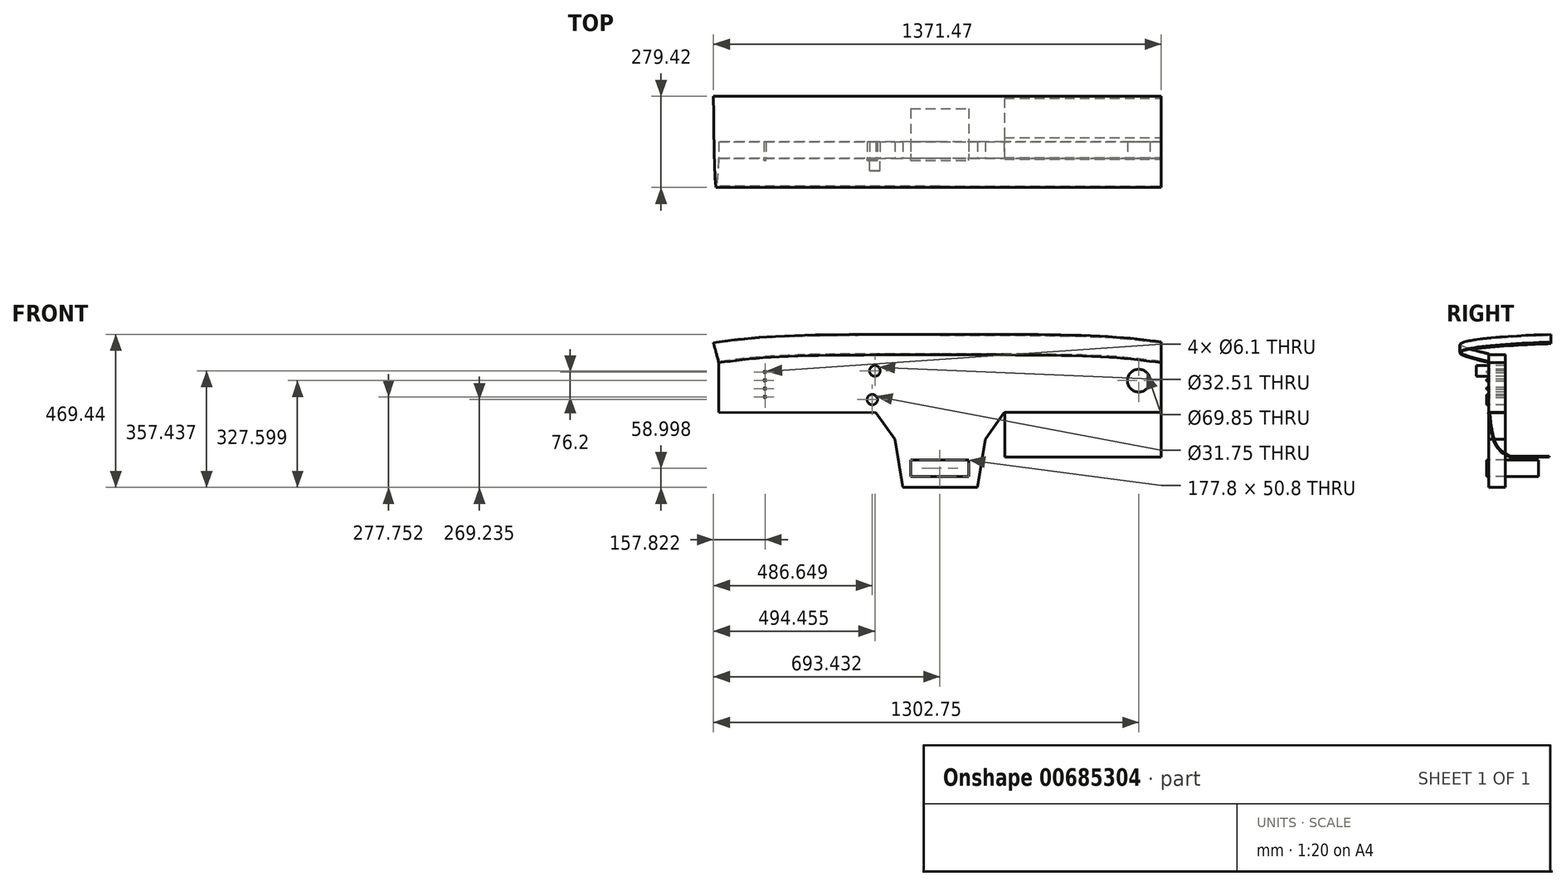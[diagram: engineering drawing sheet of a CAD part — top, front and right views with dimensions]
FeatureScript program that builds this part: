
annotation { "Feature Type Name" : "Feature", "Feature Type Description" : "" }
export const myFeature = defineFeature(function(context is Context, id is Id, definition is map)
    precondition{}
    {
        {
            var Q0;
            Q0=qCreatedBy(makeId("Front.planeOp"),FACE);
            var sketch = newSketch(context, id + "F0", { "sketchPlane" : qUnion([Q0])});
            skLineSegment(sketch, "E0.bottom", {"start": v(-257.56, -56.13) * mm, "end": v(28.19, -56.13) * mm});
            skLineSegment(sketch, "E0.top", {"start": v(-257.56, -106.93) * mm, "end": v(28.19, -106.93) * mm});
            skLineSegment(sketch, "E0.left", {"start": v(-257.56, -56.13) * mm, "end": v(-257.56, -106.93) * mm});
            skLineSegment(sketch, "E0.right", {"start": v(28.19, -56.13) * mm, "end": v(28.19, -106.93) * mm});
            skCircle(sketch, "E1", {"center": v(-226.15, -8.02) * mm, "radius": 26.2 * mm});
            skCircle(sketch, "E2", {"center": v(-154.96, -8.02) * mm, "radius": 26.2 * mm});
            skCircle(sketch, "E3", {"center": v(-83.6, -8.02) * mm, "radius": 26.2 * mm});
            skCircle(sketch, "E4", {"center": v(-11.74, -8.01) * mm, "radius": 26.2 * mm});
            skPoint(sketch, "E5.startSnap0", {"position": v(-118.95, 106.5) * mm});
            skCircle(sketch, "E6", {"center": v(-727.7, 27.7) * mm, "radius": 34.93 * mm});
            skCircle(sketch, "E7", {"center": v(-567.92, 12.4) * mm, "radius": 50.8 * mm});
            skCircle(sketch, "E8", {"center": v(-423.48, 13.97) * mm, "radius": 50.8 * mm});
            skPoint(sketch, "E9.visualSharp", {"position": v(-299.01, -120.46) * mm});
            skPoint(sketch, "E10.visualSharp", {"position": v(72.46, -120.46) * mm});
            skLineSegment(sketch, "E11.bottom", {"start": v(-271.26, 87.77) * mm, "end": v(33.54, 87.77) * mm});
            skLineSegment(sketch, "E11.top", {"start": v(-271.26, 27.37) * mm, "end": v(33.54, 27.37) * mm});
            skLineSegment(sketch, "E11.left", {"start": v(-271.26, 87.77) * mm, "end": v(-271.26, 27.37) * mm});
            skLineSegment(sketch, "E11.right", {"start": v(33.54, 87.77) * mm, "end": v(33.54, 27.37) * mm});
            skCircle(sketch, "E12", {"center": v(-655.14, 54.05) * mm, "radius": 3.05 * mm});
            skCircle(sketch, "E13", {"center": v(-655.14, 28.65) * mm, "radius": 3.05 * mm});
            skCircle(sketch, "E14", {"center": v(-655.14, 3.25) * mm, "radius": 3.05 * mm});
            skCircle(sketch, "E15", {"center": v(-655.14, -22.15) * mm, "radius": 3.05 * mm});
            skCircle(sketch, "E16", {"center": v(-318.5, 57.54) * mm, "radius": 16.25 * mm});
            skLineSegment(sketch, "E17.bottom", {"start": v(-208.43, -215.5) * mm, "end": v(-30.63, -215.5) * mm});
            skLineSegment(sketch, "E17.top", {"start": v(-208.43, -266.3) * mm, "end": v(-30.63, -266.3) * mm});
            skLineSegment(sketch, "E17.left", {"start": v(-208.43, -215.5) * mm, "end": v(-208.43, -266.3) * mm});
            skLineSegment(sketch, "E17.right", {"start": v(-30.63, -215.5) * mm, "end": v(-30.63, -266.3) * mm});
            skPoint(sketch, "E18.startSnap0", {"position": v(-118.86, 27.37) * mm});
            skLineSegment(sketch, "E19", {"start": v(-118.95, -299.9) * mm, "end": v(-233.25, -299.9) * mm});
            skLineSegment(sketch, "E20", {"start": v(-796.41, -69.66) * mm, "end": v(-315.23, -70.42) * mm});
            skLineSegment(sketch, "E21", {"start": v(-315.23, -70.42) * mm, "end": v(-257.56, -151.8) * mm});
            skLineSegment(sketch, "E22", {"start": v(-257.56, -151.8) * mm, "end": v(-233.25, -299.9) * mm});
            skLineSegment(sketch, "E23.MirrorCS", {"start": v(77.33, -70.42) * mm, "end": v(19.66, -151.8) * mm});
            skLineSegment(sketch, "E24.MirrorCS", {"start": v(19.66, -151.8) * mm, "end": v(-4.65, -299.9) * mm});
            skLineSegment(sketch, "E25.MirrorCS", {"start": v(-118.95, -299.9) * mm, "end": v(-4.65, -299.9) * mm});
            skLineSegment(sketch, "E26.MirrorCS", {"start": v(558.5, -69.66) * mm, "end": v(77.33, -70.42) * mm});
            skFitSpline(sketch, "E27", {"points": [v(-118.95, 106.5) * mm, v(-624.64, 100) * mm, v(-796.41, 82.73) * mm], "startDerivative": vector(-906.98, 1.22) * mm, "endDerivative": vector(-403.93, -53.55) * mm});
            skLineSegment(sketch, "E28", {"start": v(-796.41, 82.73) * mm, "end": v(-796.41, -69.66) * mm});
            skFitSpline(sketch, "E29.MirrorCS", {"points": [v(-118.95, 106.5) * mm, v(386.73, 100) * mm, v(558.5, 82.73) * mm], "startDerivative": vector(906.98, 1.22) * mm, "endDerivative": vector(403.93, -53.55) * mm});
            skLineSegment(sketch, "E30.MirrorCS", {"start": v(558.5, 82.73) * mm, "end": v(558.5, -69.66) * mm});
            skCircle(sketch, "E31.MirrorC", {"center": v(489.79, 27.7) * mm, "radius": 34.93 * mm});
            skCircle(sketch, "E32", {"center": v(-326.31, -30.67) * mm, "radius": 15.88 * mm});
            skLineSegment(sketch, "E33", {"start": v(-118.95, 106.5) * mm, "end": v(-118.95, 70.81) * mm});
            skSolve(sketch);
        }
        {
            var Q0;
            Q0=makeQuery(id+"F0.imprint","IMPRINT",FACE,{"disambiguationData":[TD([[makeQuery(id+"F0.imprint","IMPRINT",EDGE,{"derivedFrom":sQuery(id+"F0.wireOp",EDGE,"E6")}),1.0]])]});
            var Q1;
            Q1=makeQuery(id+"F0.imprint","IMPRINT",FACE,{"disambiguationData":[TD([[makeQuery(id+"F0.imprint","IMPRINT",EDGE,{"derivedFrom":sQuery(id+"F0.wireOp",EDGE,"E7")}),1.0]])]});
            var Q2;
            Q2=makeQuery(id+"F0.imprint","IMPRINT",FACE,{"disambiguationData":[TD([[makeQuery(id+"F0.imprint","IMPRINT",EDGE,{"derivedFrom":sQuery(id+"F0.wireOp",EDGE,"E8")}),1.0]])]});
            var Q3;
            Q3=makeQuery(id+"F0.imprint","IMPRINT",FACE,{"disambiguationData":[TD([[makeQuery(id+"F0.imprint","IMPRINT",EDGE,{"derivedFrom":sQuery(id+"F0.wireOp",EDGE,"E11.bottom")}),-1.0]])]});
            var Q4;
            Q4=makeQuery(id+"F0.imprint","IMPRINT",FACE,{"disambiguationData":[TD([[makeQuery(id+"F0.imprint","IMPRINT",EDGE,{"derivedFrom":sQuery(id+"F0.wireOp",EDGE,"E1")}),1.0]])]});
            var Q5;
            Q5=makeQuery(id+"F0.imprint","IMPRINT",FACE,{"disambiguationData":[TD([[makeQuery(id+"F0.imprint","IMPRINT",EDGE,{"derivedFrom":sQuery(id+"F0.wireOp",EDGE,"E2")}),1.0]])]});
            var Q6;
            Q6=makeQuery(id+"F0.imprint","IMPRINT",FACE,{"disambiguationData":[TD([[makeQuery(id+"F0.imprint","IMPRINT",EDGE,{"derivedFrom":sQuery(id+"F0.wireOp",EDGE,"E3")}),1.0]])]});
            var Q7;
            Q7=makeQuery(id+"F0.imprint","IMPRINT",FACE,{"disambiguationData":[TD([[makeQuery(id+"F0.imprint","IMPRINT",EDGE,{"derivedFrom":sQuery(id+"F0.wireOp",EDGE,"E4")}),1.0]])]});
            var Q8;
            Q8=makeQuery(id+"F0.imprint","IMPRINT",FACE,{"disambiguationData":[TD([[makeQuery(id+"F0.imprint","IMPRINT",EDGE,{"derivedFrom":sQuery(id+"F0.wireOp",EDGE,"E31.MirrorC")}),-1.0]])]});
            var Q9;
            Q9=makeQuery(id+"F0.imprint","IMPRINT",FACE,{"disambiguationData":[TD([[makeQuery(id+"F0.imprint","IMPRINT",EDGE,{"derivedFrom":sQuery(id+"F0.wireOp",EDGE,"E0.bottom")}),-1.0]])]});
            extrude(context, id + "F1", {"entities" : qUnion([Q0, Q1, Q2, Q3, Q4, Q5, Q6, Q7, Q8, Q9]), "oppositeDirection" : true, "depth" : 50.8 * mm, "offsetDistance" : 25.4 * mm});
        }
        {
            var Q0;
            Q0=makeQuery(id+"F0.imprint","IMPRINT",FACE,{"disambiguationData":[TD([[makeQuery(id+"F0.imprint","IMPRINT",EDGE,{"derivedFrom":sQuery(id+"F0.wireOp",EDGE,"E6")}),-1.0]])]});
            var Q1;
            Q1=makeQuery(id+"F0.imprint","IMPRINT",FACE,{"disambiguationData":[TD([[makeQuery(id+"F0.imprint","IMPRINT",EDGE,{"derivedFrom":sQuery(id+"F0.wireOp",EDGE,"26183028-2932-47e3-b212-7d85a58e5e170.MirrorC")}),1.0]])]});
            var Q2;
            Q2=makeQuery(id+"F0.imprint","IMPRINT",FACE,{"disambiguationData":[TD([[makeQuery(id+"F0.imprint","IMPRINT",EDGE,{"derivedFrom":sQuery(id+"F0.wireOp",EDGE,"E1")}),-1.0]])]});
            var Q3;
            {var subQ0=sQuery(id+"F0.wireOp",EDGE,"Lr24YdQz-NA7F-vP8l-lZQv-dD6ceGB6U4Bq");var subQ3=sQuery(id+"F0.wireOp",EDGE,"AdgguoAx-7lrN-97jz-AZlA-xOodr6nNh4v9");var subQ5=makeQuery(id+"F0.imprint","INTERSECT",VERTEX,{"derivedFrom":[subQ0,subQ3]});Q3=makeQuery(id+"F0.imprint","IMPRINT",FACE,{"disambiguationData":[TD([[makeQuery(id+"F0.imprint","IMPRINT",EDGE,{"disambiguationData":[TD([[subQ5,1.0]])],"derivedFrom":subQ3}),-1.0]])]});}
            var Q4;
            Q4=makeQuery(id+"F0.imprint","IMPRINT",FACE,{"disambiguationData":[TD([[makeQuery(id+"F0.imprint","IMPRINT",EDGE,{"derivedFrom":sQuery(id+"F0.wireOp",EDGE,"E0.bottom")}),1.0]])]});
            var Q5;
            {var subQ0=sQuery(id+"F0.wireOp",EDGE,"lboKylBz-wg3H-TF9z-j1dq-gTXtzQHKIuxb");var subQ1=sQuery(id+"F0.wireOp",EDGE,"EBcDoDZH-Jfvx-AnNu-obtp-yvls1MBHouOS");var subQ2=makeQuery(id+"F0.imprint","INTERSECT",VERTEX,{"derivedFrom":[subQ1,subQ0]});Q5=makeQuery(id+"F0.imprint","IMPRINT",FACE,{"disambiguationData":[TD([[makeQuery(id+"F0.imprint","IMPRINT",EDGE,{"disambiguationData":[TD([[subQ2,1.0]])],"derivedFrom":subQ1}),-1.0]])]});}
            var Q6;
            {var subQ5=sQuery(id+"F0.wireOp",EDGE,"UINDycS2-73tQ-8rtl-gtWs-m5Ii6CsL3kLx");Q6=makeQuery(id+"F0.imprint","IMPRINT",FACE,{"disambiguationData":[TD([[makeQuery(id+"F0.imprint","IMPRINT",EDGE,{"derivedFrom":subQ5}),1.0]])]});}
            extrude(context, id + "F2", {"entities" : qUnion([Q0, Q1, Q2, Q3, Q4, Q5, Q6]), "oppositeDirection" : true, "depth" : 2.54 * mm, "offsetDistance" : 25.4 * mm});
        }
        {
            var Q0;
            Q0=makeQuery(id+"F0.imprint","IMPRINT",FACE,{"disambiguationData":[TD([[makeQuery(id+"F0.imprint","IMPRINT",EDGE,{"derivedFrom":sQuery(id+"F0.wireOp",EDGE,"E12")}),1.0]])]});
            var Q1;
            Q1=makeQuery(id+"F0.imprint","IMPRINT",FACE,{"disambiguationData":[TD([[makeQuery(id+"F0.imprint","IMPRINT",EDGE,{"derivedFrom":sQuery(id+"F0.wireOp",EDGE,"E13")}),1.0]])]});
            var Q2;
            Q2=makeQuery(id+"F0.imprint","IMPRINT",FACE,{"disambiguationData":[TD([[makeQuery(id+"F0.imprint","IMPRINT",EDGE,{"derivedFrom":sQuery(id+"F0.wireOp",EDGE,"E14")}),1.0]])]});
            var Q3;
            Q3=makeQuery(id+"F0.imprint","IMPRINT",FACE,{"disambiguationData":[TD([[makeQuery(id+"F0.imprint","IMPRINT",EDGE,{"derivedFrom":sQuery(id+"F0.wireOp",EDGE,"E15")}),1.0]])]});
            extrude(context, id + "F3", {"entities" : qUnion([Q0, Q1, Q2, Q3]), "depth" : 6.35 * mm, "offsetDistance" : 25.4 * mm});
        }
        {
            var Q0;
            Q0=makeQuery(id+"F0.imprint","IMPRINT",FACE,{"disambiguationData":[TD([[makeQuery(id+"F0.imprint","IMPRINT",EDGE,{"derivedFrom":sQuery(id+"F0.wireOp",EDGE,"E16")}),1.0]])]});
            extrude(context, id + "F4", {"entities" : qUnion([Q0]), "depth" : 38.1 * mm, "offsetDistance" : 25.4 * mm});
        }
        {
            var Q0;
            Q0=makeQuery(id+"F0.imprint","IMPRINT",FACE,{"disambiguationData":[TD([[makeQuery(id+"F0.imprint","IMPRINT",EDGE,{"derivedFrom":sQuery(id+"F0.wireOp",EDGE,"E17.bottom")}),-1.0]])]});
            extrude(context, id + "F5", {"entities" : qUnion([Q0]), "oppositeDirection" : true, "depth" : 152.4 * mm, "offsetDistance" : 25.4 * mm});
        }
        {
            var Q0;
            {var subQ0=sQuery(id+"F0.wireOp",EDGE,"E17.left");Q0=makeQuery(id+"F0.imprint","IMPRINT",FACE,{"disambiguationData":[TD([[makeQuery(id+"F0.imprint","IMPRINT",EDGE,{"derivedFrom":subQ0}),1.0]])]});}
            var Q1;
            {var subQ0=sQuery(id+"F0.wireOp",EDGE,"E17.right");Q1=makeQuery(id+"F0.imprint","IMPRINT",FACE,{"disambiguationData":[TD([[makeQuery(id+"F0.imprint","IMPRINT",EDGE,{"derivedFrom":subQ0}),-1.0]])]});}
            extrude(context, id + "F6", {"entities" : qUnion([Q0, Q1]), "depth" : 6.35 * mm, "offsetDistance" : 25.4 * mm});
        }
        {
            var Q0;
            {var subQ0=sQuery(id+"F0.wireOp",EDGE,"E17.right");Q0=makeQuery(id+"F0.imprint","IMPRINT",FACE,{"disambiguationData":[TD([[makeQuery(id+"F0.imprint","IMPRINT",EDGE,{"derivedFrom":subQ0}),-1.0]])]});}
            var Q1;
            {var subQ0=sQuery(id+"F0.wireOp",EDGE,"E17.left");Q1=makeQuery(id+"F0.imprint","IMPRINT",FACE,{"disambiguationData":[TD([[makeQuery(id+"F0.imprint","IMPRINT",EDGE,{"derivedFrom":subQ0}),1.0]])]});}
            extrude(context, id + "F7", {"entities" : qUnion([Q0, Q1]), "oppositeDirection" : true, "depth" : 127 * mm, "offsetDistance" : 25.4 * mm});
        }
        {
            var Q0;
            Q0=makeQuery(id+"F7.opExtrude","SWEPT_BODY",BODY,{"disambiguationData":[OSD([sQuery(id+"F0.wireOp",EDGE,"E17.bottom"),sQuery(id+"F0.wireOp",EDGE,"E17.top"),sQuery(id+"F0.wireOp",EDGE,"E17.left"),sQuery(id+"F0.wireOp",EDGE,"E17.right")])]});
            deleteBodies(context, id + "F8", {"entities" : qUnion([Q0])});
        }
        {
            var Q0;
            Q0=makeQuery(id+"F2.opExtrude","SWEPT_FACE",FACE,{"disambiguationData":[OSD([sQuery(id+"F0.wireOp",EDGE,"E30.MirrorCS")])]});
            var sketch = newSketch(context, id + "F9", { "sketchPlane" : qUnion([Q0])});
            skFitSpline(sketch, "E34", {"points": [v(0, 82.73) * mm, v(-88.9, 114.48) * mm, v(190.5, 146.23) * mm], "startDerivative": vector(-367.73, 93.23) * mm, "endDerivative": vector(656.01, 21.95) * mm});
            skFitSpline(sketch, "E35", {"points": [v(-0.04, 86.36) * mm, v(-81.2, 118.3) * mm, v(190.26, 143.17) * mm, v(190.5, 143.17) * mm], "startDerivative": vector(-413.73, 96.83) * mm, "endDerivative": vector(2.14, -0.62) * mm});
            skLineSegment(sketch, "E36", {"start": v(190.5, 146.23) * mm, "end": v(190.5, 143.17) * mm});
            skLineSegment(sketch, "E37", {"start": v(-0.04, 86.36) * mm, "end": v(0, 82.73) * mm});
            skSolve(sketch);
        }
        {
            var Q0;
            Q0=makeQuery(id+"F0.imprint","IMPRINT",FACE,{"disambiguationData":[TD([[makeQuery(id+"F0.imprint","IMPRINT",EDGE,{"derivedFrom":sQuery(id+"F0.wireOp",EDGE,"E32")}),1.0]])]});
            extrude(context, id + "F10", {"entities" : qUnion([Q0]), "depth" : 6.35 * mm, "offsetDistance" : 25.4 * mm});
        }
        {
            var Q0;
            Q0=makeQuery(id+"F9.imprint","IMPRINT",FACE,{"disambiguationData":[TD([[makeQuery(id+"F9.imprint","IMPRINT",EDGE,{"derivedFrom":sQuery(id+"F9.wireOp",EDGE,"E34")}),-1.0]])]});
            var Q1;
            Q1=sQuery(id+"F0.wireOp",EDGE,"E29.MirrorCS");
            var Q2;
            Q2=sQuery(id+"F0.wireOp",EDGE,"E27");
            sweep(context, id + "F11", {"profiles" : qUnion([Q0]), "path" : qUnion([Q1, Q2])});
        }
        {
            var Q0;
            {var subQ0=sQuery(id+"F0.wireOp",EDGE,"E30.MirrorCS");Q0=makeQuery(id+"F9.imprint","IMPRINT",FACE,{"disambiguationData":[TD([[makeQuery(id+"F9.imprint","IMPRINT",EDGE,{"derivedFrom":makeQuery(id+"F2.opExtrude","CAP_EDGE",EDGE,{"disambiguationData":[OSD([subQ0])],"isStart":true})}),1.0]])]});}
            var sketch = newSketch(context, id + "F12", { "sketchPlane" : qUnion([Q0])});
            skLineSegment(sketch, "E38", {"start": v(63.79, -206.88) * mm, "end": v(184.22, -206.88) * mm});
            skFitSpline(sketch, "E39", {"points": [v(-1.35, -69.1) * mm, v(15.86, -159.53) * mm, v(63.79, -206.88) * mm], "startDerivative": vector(21.45, -153.91) * mm, "endDerivative": vector(184.24, -92.68) * mm});
            skFitSpline(sketch, "E40", {"points": [v(2.49, -69.25) * mm, v(18.5, -157.67) * mm, v(64.6, -204.18) * mm], "startDerivative": vector(18.22, -186.03) * mm, "endDerivative": vector(166.33, -80.06) * mm});
            skLineSegment(sketch, "E41", {"start": v(-1.35, -69.1) * mm, "end": v(2.49, -69.25) * mm});
            skLineSegment(sketch, "E42", {"start": v(64.6, -204.18) * mm, "end": v(184.29, -204.18) * mm});
            skLineSegment(sketch, "E43", {"start": v(184.29, -204.18) * mm, "end": v(184.22, -206.88) * mm});
            skSolve(sketch);
        }
        {
            var Q0;
            Q0 = qSketchRegion(id + "F12", true);
            extrude(context, id + "F13", {"entities" : qUnion([Q0]), "operationType" : NewBodyOperationType.ADD, "oppositeDirection" : true, "depth" : 479.3 * mm, "offsetDistance" : 25.4 * mm});
        }
    });
